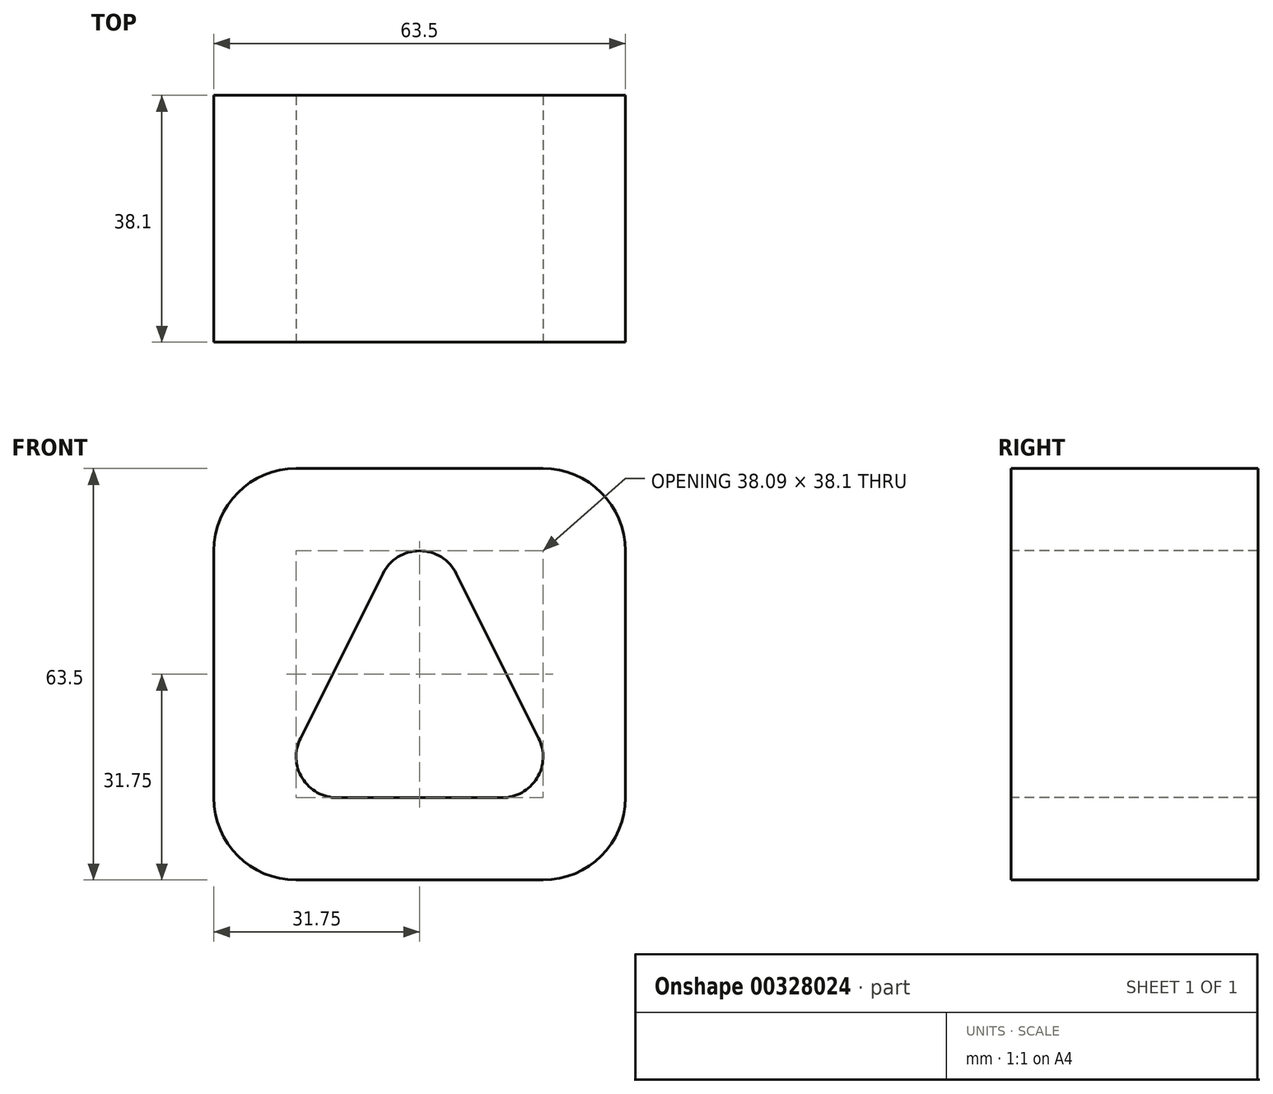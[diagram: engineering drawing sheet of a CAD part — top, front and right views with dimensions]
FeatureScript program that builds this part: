
annotation { "Feature Type Name" : "Feature", "Feature Type Description" : "" }
export const myFeature = defineFeature(function(context is Context, id is Id, definition is map)
    precondition{}
    {
        {
            var Q0;
            Q0=qCreatedBy(makeId("Front.planeOp"),FACE);
            var sketch = newSketch(context, id + "F0", { "sketchPlane" : qUnion([Q0])});
            skLineSegment(sketch, "E0", {"start": v(0, 0) * mm, "end": v(63.5, 0) * mm});
            skLineSegment(sketch, "E1", {"start": v(63.5, 0) * mm, "end": v(63.5, 63.5) * mm});
            skLineSegment(sketch, "E2", {"start": v(63.5, 63.5) * mm, "end": v(0, 63.5) * mm});
            skLineSegment(sketch, "E3", {"start": v(0, 63.5) * mm, "end": v(0, 0) * mm});
            skArc(sketch, "E4", {"start": v(13.37, 21.89) * mm, "mid": v(13.65, 15.71) * mm, "end": v(19.05, 12.7) * mm});
            skArc(sketch, "E5", {"start": v(37.43, 47.29) * mm, "mid": v(31.75, 50.8) * mm, "end": v(26.07, 47.29) * mm});
            skArc(sketch, "E6", {"start": v(44.45, 12.7) * mm, "mid": v(49.85, 15.71) * mm, "end": v(50.13, 21.89) * mm});
            skLineSegment(sketch, "E7", {"start": v(37.43, 47.29) * mm, "end": v(50.13, 21.89) * mm});
            skLineSegment(sketch, "E8", {"start": v(44.45, 12.7) * mm, "end": v(19.05, 12.7) * mm});
            skLineSegment(sketch, "E9", {"start": v(13.37, 21.89) * mm, "end": v(26.07, 47.29) * mm});
            skSolve(sketch);
        }
        {
            var Q0;
            Q0=makeQuery(id+"F0.imprint","IMPRINT",FACE,{"disambiguationData":[TD([[makeQuery(id+"F0.imprint","IMPRINT",EDGE,{"derivedFrom":sQuery(id+"F0.wireOp",EDGE,"E0")}),1.0]])]});
            extrude(context, id + "F1", {"entities" : qUnion([Q0]), "oppositeDirection" : true, "depth" : 38.1 * mm});
        }
        {
            var Q0;
            Q0=makeQuery(id+"F1.opExtrude","SWEPT_EDGE",EDGE,{"disambiguationData":[OSD([sQuery(id+"F0.wireOp",EDGE,"E1"),sQuery(id+"F0.wireOp",EDGE,"E2")])]});
            var Q1;
            Q1=makeQuery(id+"F1.opExtrude","SWEPT_EDGE",EDGE,{"disambiguationData":[OSD([sQuery(id+"F0.wireOp",EDGE,"E0"),sQuery(id+"F0.wireOp",EDGE,"E1")])]});
            var Q2;
            Q2=makeQuery(id+"F1.opExtrude","SWEPT_EDGE",EDGE,{"disambiguationData":[OSD([sQuery(id+"F0.wireOp",EDGE,"E0"),sQuery(id+"F0.wireOp",EDGE,"E3")])]});
            var Q3;
            Q3=makeQuery(id+"F1.opExtrude","SWEPT_EDGE",EDGE,{"disambiguationData":[OSD([sQuery(id+"F0.wireOp",EDGE,"E2"),sQuery(id+"F0.wireOp",EDGE,"E3")])]});
            fillet(context, id + "F2", {"entities" : qUnion([Q0, Q1, Q2, Q3]), "radius" : 12.7 * mm, "tangentPropagation" : true, "allowEdgeOverflow" : false});
        }
    });
